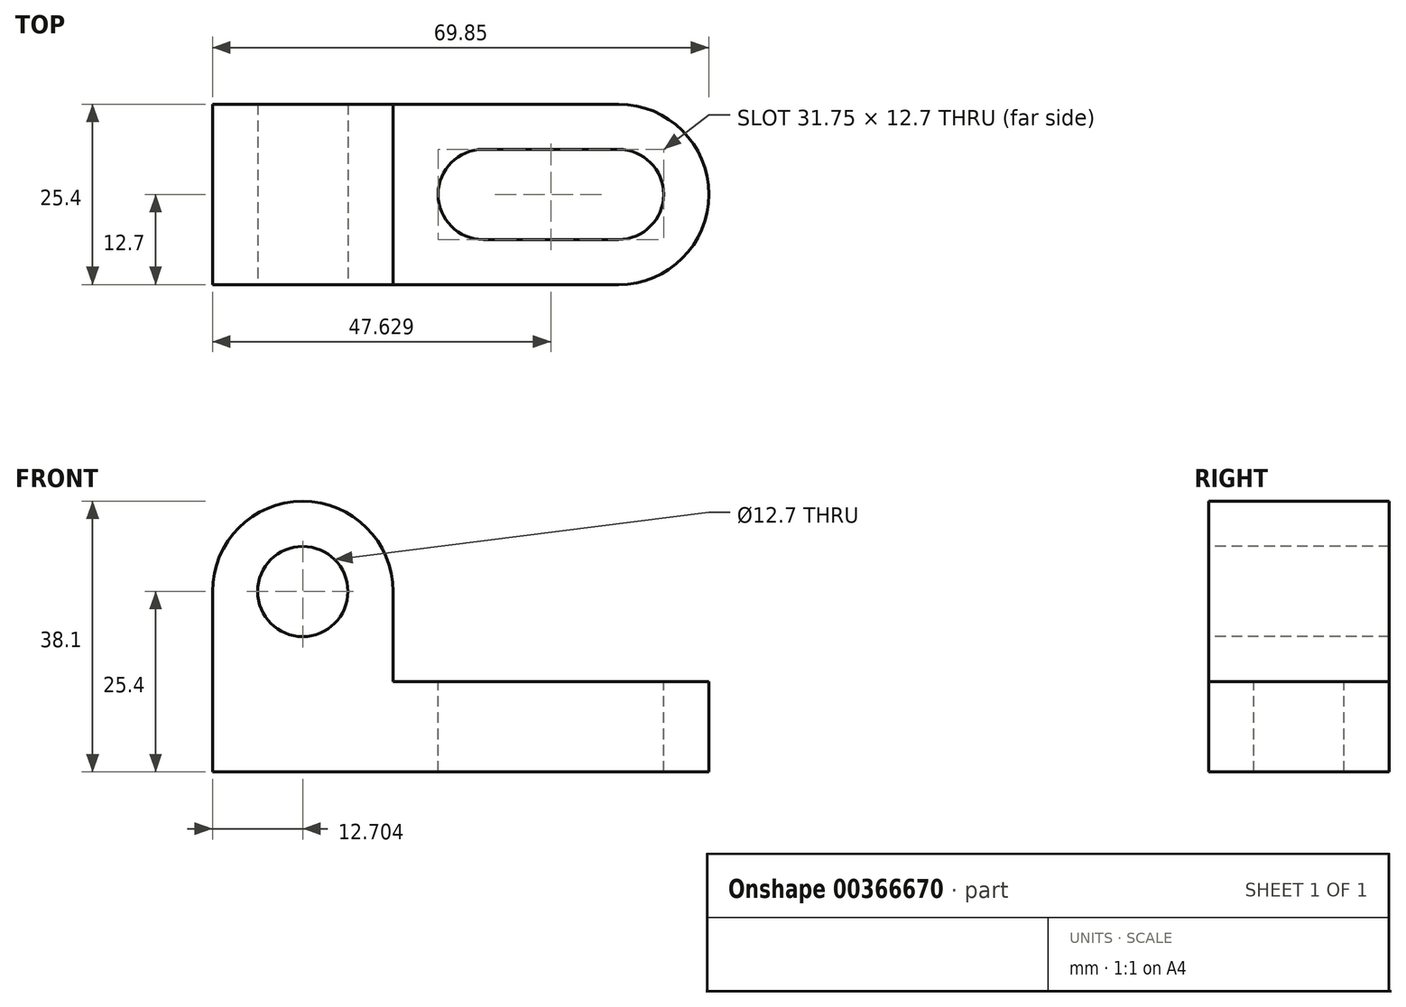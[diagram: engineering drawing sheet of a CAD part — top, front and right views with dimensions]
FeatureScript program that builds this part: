
annotation { "Feature Type Name" : "Feature", "Feature Type Description" : "" }
export const myFeature = defineFeature(function(context is Context, id is Id, definition is map)
    precondition{}
    {
        {
            var Q0;
            Q0=qCreatedBy(makeId("Front.planeOp"),FACE);
            var sketch = newSketch(context, id + "F0", { "sketchPlane" : qUnion([Q0])});
            skLineSegment(sketch, "E0", {"start": v(-72.38, 0) * mm, "end": v(-72.38, 38.1) * mm});
            skLineSegment(sketch, "E1", {"start": v(-72.38, 38.1) * mm, "end": v(-2.53, 38.1) * mm});
            skLineSegment(sketch, "E2", {"start": v(-2.53, 38.1) * mm, "end": v(-2.53, 0) * mm});
            skLineSegment(sketch, "E3", {"start": v(-2.53, 0) * mm, "end": v(-72.38, 0) * mm});
            skSolve(sketch);
        }
        {
            var Q0;
            Q0=makeQuery(id+"F0.imprint","IMPRINT",FACE,{"disambiguationData":[TD([[makeQuery(id+"F0.imprint","IMPRINT",EDGE,{"derivedFrom":sQuery(id+"F0.wireOp",EDGE,"E0")}),-1.0]])]});
            extrude(context, id + "F1", {"entities" : qUnion([Q0]), "depth" : 25.4 * mm});
        }
        {
            var Q0;
            Q0=makeQuery(id+"F1.opExtrude","CAP_FACE",FACE,{"disambiguationData":[OSD([sQuery(id+"F0.wireOp",EDGE,"E0"),sQuery(id+"F0.wireOp",EDGE,"E1"),sQuery(id+"F0.wireOp",EDGE,"E2"),sQuery(id+"F0.wireOp",EDGE,"E3")])],"isStart":false});
            var sketch = newSketch(context, id + "F2", { "sketchPlane" : qUnion([Q0])});
            skLineSegment(sketch, "E4", {"start": v(-46.98, 38.1) * mm, "end": v(-46.98, 12.7) * mm});
            skLineSegment(sketch, "E5", {"start": v(-46.98, 12.7) * mm, "end": v(-2.53, 12.7) * mm});
            skSolve(sketch);
        }
        {
            var Q0;
            {var subQ0=sQuery(id+"F2.wireOp",EDGE,"E4");Q0=makeQuery(id+"F2.imprint","IMPRINT",FACE,{"disambiguationData":[TD([[makeQuery(id+"F2.imprint","IMPRINT",EDGE,{"derivedFrom":subQ0}),1.0]])]});}
            extrude(context, id + "F3", {"entities" : qUnion([Q0]), "operationType" : NewBodyOperationType.REMOVE, "oppositeDirection" : true, "depth" : 25.4 * mm});
        }
        {
            var Q0;
            Q0=makeQuery(id+"F1.opExtrude","CAP_FACE",FACE,{"disambiguationData":[OSD([sQuery(id+"F0.wireOp",EDGE,"E0"),sQuery(id+"F0.wireOp",EDGE,"E1"),sQuery(id+"F0.wireOp",EDGE,"E2"),sQuery(id+"F0.wireOp",EDGE,"E3")])],"isStart":false});
            var sketch = newSketch(context, id + "F4", { "sketchPlane" : qUnion([Q0])});
            skCircle(sketch, "E6", {"center": v(-59.68, 25.4) * mm, "radius": 6.35 * mm});
            skArc(sketch, "E7", {"start": v(-46.98, 25.4) * mm, "mid": v(-59.68, 38.1) * mm, "end": v(-72.38, 25.4) * mm});
            skSolve(sketch);
        }
        {
            var Q0;
            {var subQ0=sQuery(id+"F4.wireOp",EDGE,"E7");var subQ1=makeQuery(id+"F1.opExtrude","CAP_EDGE",EDGE,{"disambiguationData":[OSD([sQuery(id+"F0.wireOp",EDGE,"E0")])],"isStart":false});var subQ2=makeQuery(id+"F4.imprint","INTERSECT",VERTEX,{"derivedFrom":[subQ1,subQ0]});Q0=makeQuery(id+"F4.imprint","IMPRINT",FACE,{"disambiguationData":[TD([[makeQuery(id+"F4.imprint","IMPRINT",EDGE,{"disambiguationData":[TD([[subQ2,1.0]])],"derivedFrom":subQ0}),-1.0]])]});}
            var Q1;
            {var subQ0=sQuery(id+"F4.wireOp",EDGE,"E7");var subQ1=makeQuery(id+"F3.boolean.opBoolean","COPY",EDGE,{"derivedFrom":makeQuery(id+"F3.opExtrude","CAP_EDGE",EDGE,{"disambiguationData":[OSD([sQuery(id+"F2.wireOp",EDGE,"E4")])],"isStart":true})});var subQ2=makeQuery(id+"F4.imprint","INTERSECT",VERTEX,{"derivedFrom":[subQ1,subQ0]});Q1=makeQuery(id+"F4.imprint","IMPRINT",FACE,{"disambiguationData":[TD([[makeQuery(id+"F4.imprint","IMPRINT",EDGE,{"disambiguationData":[TD([[subQ2,-1.0]])],"derivedFrom":subQ0}),-1.0]])]});}
            var Q2;
            Q2=makeQuery(id+"F4.imprint","IMPRINT",FACE,{"disambiguationData":[TD([[makeQuery(id+"F4.imprint","IMPRINT",EDGE,{"derivedFrom":sQuery(id+"F4.wireOp",EDGE,"E6")}),1.0]])]});
            extrude(context, id + "F5", {"entities" : qUnion([Q0, Q1, Q2]), "operationType" : NewBodyOperationType.REMOVE, "oppositeDirection" : true, "depth" : 25.4 * mm});
        }
        {
            var Q0;
            Q0=makeQuery(id+"F3.boolean.opBoolean","COPY",FACE,{"derivedFrom":makeQuery(id+"F3.opExtrude","SWEPT_FACE",FACE,{"disambiguationData":[OSD([sQuery(id+"F2.wireOp",EDGE,"E5")])]})});
            var sketch = newSketch(context, id + "F6", { "sketchPlane" : qUnion([Q0])});
            skCircle(sketch, "E8", {"center": v(-34.28, -12.7) * mm, "radius": 6.35 * mm});
            skCircle(sketch, "E9", {"center": v(-15.23, -12.7) * mm, "radius": 6.35 * mm});
            skLineSegment(sketch, "E10", {"start": v(-34.28, -6.35) * mm, "end": v(-15.23, -6.35) * mm});
            skLineSegment(sketch, "E11", {"start": v(-34.28, -19.05) * mm, "end": v(-15.23, -19.05) * mm});
            skArc(sketch, "E12", {"start": v(-15.23, -25.4) * mm, "mid": v(-2.53, -12.7) * mm, "end": v(-15.23, 0) * mm});
            skSolve(sketch);
        }
        {
            var Q0;
            {var subQ0=sQuery(id+"F6.wireOp",EDGE,"E12");var subQ1=sQuery(id+"F2.wireOp",EDGE,"E5");var subQ2=makeQuery(id+"F3.boolean.opBoolean","COPY",EDGE,{"derivedFrom":makeQuery(id+"F3.opExtrude","CAP_EDGE",EDGE,{"disambiguationData":[OSD([subQ1])],"isStart":true})});var subQ3=makeQuery(id+"F6.imprint","INTERSECT",VERTEX,{"derivedFrom":[subQ2,subQ0]});Q0=makeQuery(id+"F6.imprint","IMPRINT",FACE,{"disambiguationData":[TD([[makeQuery(id+"F6.imprint","IMPRINT",EDGE,{"disambiguationData":[TD([[subQ3,-1.0]])],"derivedFrom":subQ0}),-1.0]])]});}
            var Q1;
            {var subQ0=sQuery(id+"F6.wireOp",EDGE,"E9");var subQ1=makeQuery(id+"F6.imprint","INTERSECT",VERTEX,{"derivedFrom":[subQ0,sQuery(id+"F6.wireOp",EDGE,"E10")]});Q1=makeQuery(id+"F6.imprint","IMPRINT",FACE,{"disambiguationData":[TD([[makeQuery(id+"F6.imprint","IMPRINT",EDGE,{"disambiguationData":[TD([[subQ1,-1.0]])],"derivedFrom":subQ0}),1.0]])]});}
            var Q2;
            {var subQ0=sQuery(id+"F6.wireOp",EDGE,"E10");Q2=makeQuery(id+"F6.imprint","IMPRINT",FACE,{"disambiguationData":[TD([[makeQuery(id+"F6.imprint","IMPRINT",EDGE,{"derivedFrom":subQ0}),-1.0]])]});}
            var Q3;
            {var subQ0=sQuery(id+"F6.wireOp",EDGE,"E8");var subQ1=makeQuery(id+"F6.imprint","INTERSECT",VERTEX,{"derivedFrom":[subQ0,sQuery(id+"F6.wireOp",EDGE,"E10")]});Q3=makeQuery(id+"F6.imprint","IMPRINT",FACE,{"disambiguationData":[TD([[makeQuery(id+"F6.imprint","IMPRINT",EDGE,{"disambiguationData":[TD([[subQ1,-1.0]])],"derivedFrom":subQ0}),1.0]])]});}
            var Q4;
            {var subQ0=sQuery(id+"F6.wireOp",EDGE,"E12");var subQ1=sQuery(id+"F2.wireOp",EDGE,"E5");var subQ2=makeQuery(id+"F3.boolean.opBoolean","COPY",EDGE,{"derivedFrom":makeQuery(id+"F3.opExtrude","CAP_EDGE",EDGE,{"disambiguationData":[OSD([subQ1])],"isStart":false})});var subQ3=makeQuery(id+"F6.imprint","INTERSECT",VERTEX,{"derivedFrom":[subQ2,subQ0]});Q4=makeQuery(id+"F6.imprint","IMPRINT",FACE,{"disambiguationData":[TD([[makeQuery(id+"F6.imprint","IMPRINT",EDGE,{"disambiguationData":[TD([[subQ3,1.0]])],"derivedFrom":subQ0}),-1.0]])]});}
            extrude(context, id + "F7", {"entities" : qUnion([Q0, Q1, Q2, Q3, Q4]), "operationType" : NewBodyOperationType.REMOVE, "oppositeDirection" : true, "depth" : 25.4 * mm});
        }
    });
